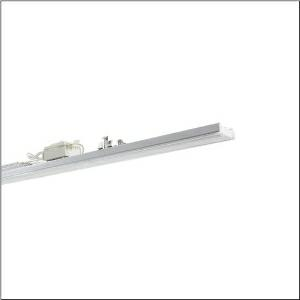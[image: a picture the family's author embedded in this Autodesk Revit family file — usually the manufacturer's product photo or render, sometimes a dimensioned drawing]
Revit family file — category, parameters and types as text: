
# Revit family: licross_r__11_recessed_ho_51tl12dv4b5m_e519
name_source: partatom
category: Lighting Fixtures
units: mm (PartAtom-declared; Revit-internal decimal feet)

## family parameters
Cut with Voids When Loaded = No
Host = Face
Light Source = No
Part Type = Normal
Room Calculation Point = No
Round Connector Dimension = Use Diameter
Shared = No

## types (1)
- --- (1 x LED, 11630 lm, 59.3 W, 4000K)
    Apparent Load = 59 VA
    CIE Flux Codes = 66 91 98 100 100
    Color Rendering = 80
    Color Temperature = 4000K
    Default Elevation = 1800 mm
    Description = Licross® 11 Recessed HO, luminaire insert, of sheet steel, coil coated, white, length: 2.250mm, width: 66mm, height: 67mm, LED rated luminous flux: 11.630lm, light colour: 840, control gear: DALI 2, with plug, 5-pole, with phase selection, mains connection: 220..240V, AC, 50/60Hz, rated input power: 59W, internal wiring halogen-free, primary optical cover: cover, of PMMA, light emission: direct distribution, primary light characteristic: symmetric, protection rating (complete): IP40, insulation class (complete): insulation class I (protective earthing), certification: CE, ENEC, VDE, UKCA, protection symbol: D if used in an environment without relevant dust loads with corresponding accessories, impact resistance: IK06, permissible ambient temperature for indoor applications: -25..+35°C, corresponds to IFS (International Featured Standards) requirements for safety and quality in the food industry, reducing of maximum allowable ambient temperature of 5°C with ceiling mounting, LABS conformity tested according to VDMA 24364:2018-05, packaging unit: 1 piece
    Height = 58 mm
    Lamp = 1 x LED
    Lamp Light Flux = 11630 lm
    Lamp Power = 59.3 W
    Lamp count = 1
    Length = 2250 mm
    Luminous efficacy = 196 lm/W
    Manufacturer = Siteco
    ModVariant = No
    Model = 51TL12DV4B5M
    Mounting Place = Ceiling
    Mounting Type = Pendant
    Number of Poles = 1
    OnlyDefault = Yes
    Power Factor = 1
    Product Name = Licross® 11 Recessed HO
    Product group = luminaire insert | ceiling pendant
    ProductGroupID = 902
    Protection Class = Protection class I
    Protection Degree = IP 40
    RLX_Detail_Level = 1
    RLX_Emergency_Light_Flux = 0 lm
    RLX_Emergency_Type = 0
    RLX_Emergency_Type_DB = No
    RlxData = <blob elided: 29165 chars, md5=45181ba8>
    Socket = socket
    Standby Power = 0 W
    System Light Flux = 11630 lm
    System Power = 59 W
    Type Comments = factory setting: luminous flux: 100 % | dim-lin: 254 | 278 mA
    Type Image = l_1296930.jpg
    URL = http://relux.com
    VarID = @adj_121041
    Voltage = 0 V
    Weight = 0.00 kg
    Width = 66 mm

## geometry (parser evidence)
native form markers: Blend x4, Sweep x10
no freeform markers — native parametric forms only
